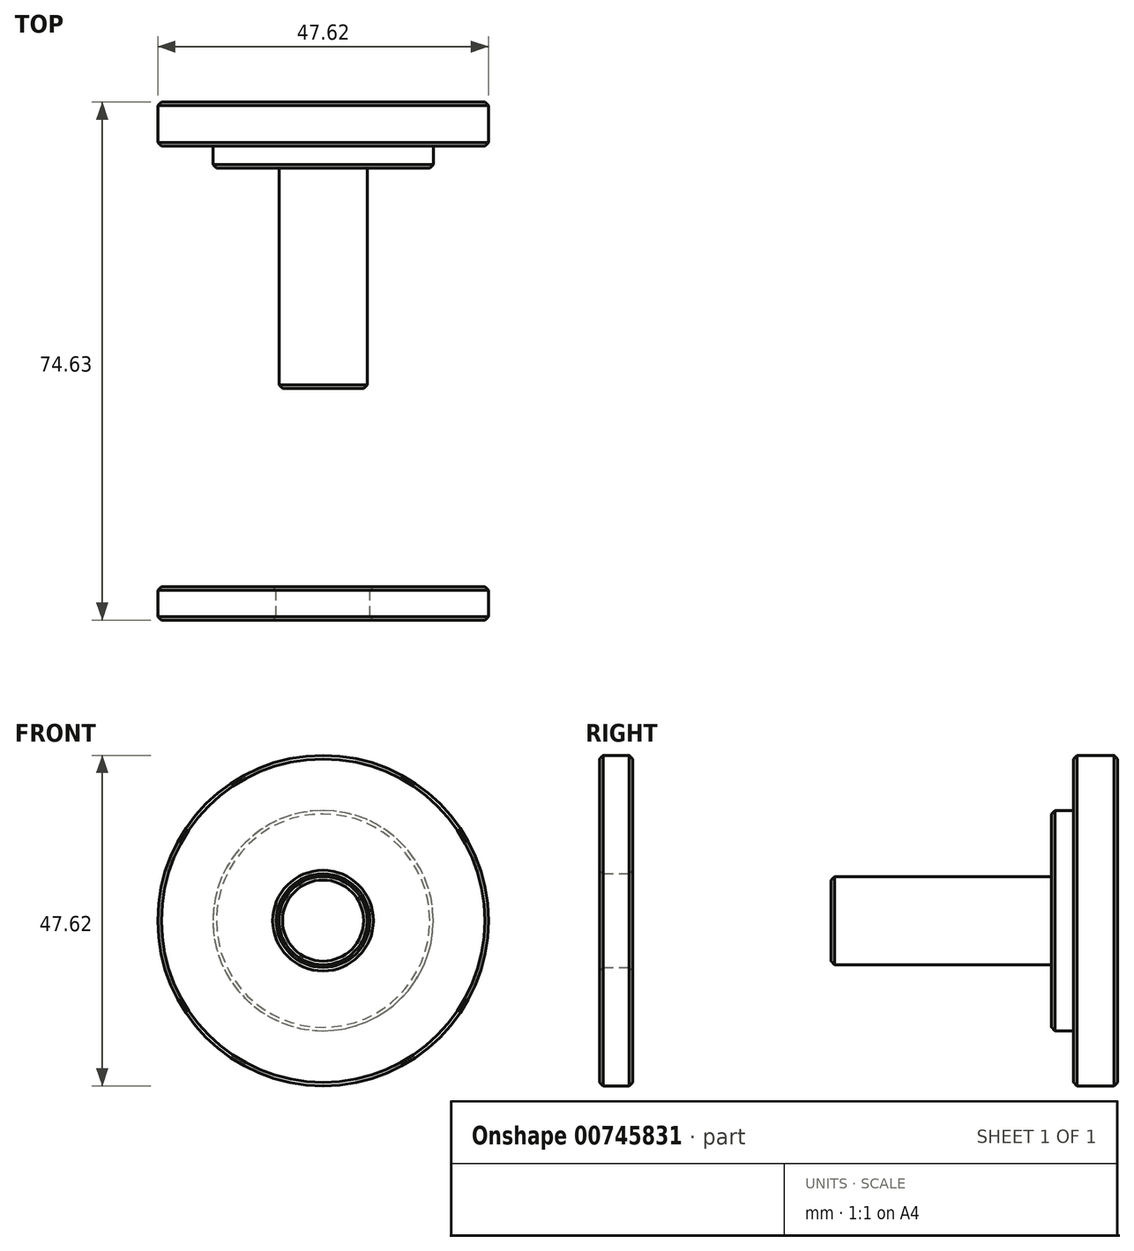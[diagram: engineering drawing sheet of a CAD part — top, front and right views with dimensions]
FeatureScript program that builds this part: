
annotation { "Feature Type Name" : "Feature", "Feature Type Description" : "" }
export const myFeature = defineFeature(function(context is Context, id is Id, definition is map)
    precondition{}
    {
        {
            var Q0;
            Q0=qCreatedBy(makeId("Top.planeOp"),FACE);
            var sketch = newSketch(context, id + "F0", { "sketchPlane" : qUnion([Q0])});
            skLineSegment(sketch, "E0", {"start": v(0, 34.93) * mm, "end": v(0, 0) * mm, "construction": true});
            skLineSegment(sketch, "E1", {"start": v(0, 0) * mm, "end": v(23.81, 0) * mm});
            skLineSegment(sketch, "E2", {"start": v(23.81, 0) * mm, "end": v(23.81, -6.35) * mm});
            skLineSegment(sketch, "E3", {"start": v(23.81, -6.35) * mm, "end": v(15.88, -6.35) * mm});
            skLineSegment(sketch, "E4", {"start": v(15.88, -6.35) * mm, "end": v(15.88, -9.53) * mm});
            skLineSegment(sketch, "E5", {"start": v(15.88, -9.53) * mm, "end": v(6.35, -9.53) * mm});
            skLineSegment(sketch, "E6", {"start": v(6.35, -9.53) * mm, "end": v(6.35, -41.28) * mm});
            skLineSegment(sketch, "E7", {"start": v(6.35, -41.28) * mm, "end": v(0, -41.28) * mm});
            skLineSegment(sketch, "E8", {"start": v(0, -41.28) * mm, "end": v(0, 0) * mm});
            skSolve(sketch);
        }
        {
            var Q0;
            Q0 = qSketchRegion(id + "F0", true);
            var Q1;
            Q1=sQuery(id+"F0.wireOp",EDGE,"E0");
            revolve(context, id + "F1", {"surfaceOperationType" : NewSurfaceOperationType.NEW, "entities" : qUnion([Q0]), "axis" : qUnion([Q1]), "revolveType" : RevolveType.FULL});
        }
        {
            var Q0;
            Q0=qCreatedBy(makeId("Top.planeOp"),FACE);
            var sketch = newSketch(context, id + "F2", { "sketchPlane" : qUnion([Q0])});
            skLineSegment(sketch, "E9", {"start": v(0, -30.05) * mm, "end": v(0, -63.76) * mm, "construction": true});
            skLineSegment(sketch, "E10.bottom", {"start": v(6.74, -69.85) * mm, "end": v(23.81, -69.85) * mm});
            skLineSegment(sketch, "E10.top", {"start": v(6.74, -74.63) * mm, "end": v(23.81, -74.63) * mm});
            skLineSegment(sketch, "E10.left", {"start": v(6.74, -69.85) * mm, "end": v(6.74, -74.63) * mm});
            skLineSegment(sketch, "E10.right", {"start": v(23.81, -69.85) * mm, "end": v(23.81, -74.63) * mm});
            skSolve(sketch);
        }
        {
            var Q0;
            Q0 = qSketchRegion(id + "F2", true);
            var Q1;
            Q1=sQuery(id+"F2.wireOp",EDGE,"E9");
            revolve(context, id + "F3", {"surfaceOperationType" : NewSurfaceOperationType.NEW, "entities" : qUnion([Q0]), "axis" : qUnion([Q1]), "revolveType" : RevolveType.FULL});
        }
        {
            var Q0;
            Q0=makeQuery(id+"F1.opRevolve","SWEPT_EDGE",EDGE,{"disambiguationData":[OSD([sQuery(id+"F0.wireOp",EDGE,"E1"),sQuery(id+"F0.wireOp",EDGE,"E2")])]});
            var Q1;
            Q1=makeQuery(id+"F1.opRevolve","SWEPT_EDGE",EDGE,{"disambiguationData":[OSD([sQuery(id+"F0.wireOp",EDGE,"E2"),sQuery(id+"F0.wireOp",EDGE,"E3")])]});
            var Q2;
            Q2=makeQuery(id+"F1.opRevolve","SWEPT_EDGE",EDGE,{"disambiguationData":[OSD([sQuery(id+"F0.wireOp",EDGE,"E4"),sQuery(id+"F0.wireOp",EDGE,"E5")])]});
            var Q3;
            Q3=makeQuery(id+"F1.opRevolve","SWEPT_EDGE",EDGE,{"disambiguationData":[OSD([sQuery(id+"F0.wireOp",EDGE,"E6"),sQuery(id+"F0.wireOp",EDGE,"E7")])]});
            var Q4;
            Q4=makeQuery(id+"F3.opRevolve","SWEPT_EDGE",EDGE,{"disambiguationData":[OSD([sQuery(id+"F2.wireOp",EDGE,"E10.bottom"),sQuery(id+"F2.wireOp",EDGE,"E10.right")])]});
            var Q5;
            Q5=makeQuery(id+"F3.opRevolve","SWEPT_EDGE",EDGE,{"disambiguationData":[OSD([sQuery(id+"F2.wireOp",EDGE,"E10.top"),sQuery(id+"F2.wireOp",EDGE,"E10.right")])]});
            var Q6;
            Q6=makeQuery(id+"F3.opRevolve","SWEPT_EDGE",EDGE,{"disambiguationData":[OSD([sQuery(id+"F2.wireOp",EDGE,"E10.top"),sQuery(id+"F2.wireOp",EDGE,"E10.left")])]});
            var Q7;
            Q7=makeQuery(id+"F3.opRevolve","SWEPT_EDGE",EDGE,{"disambiguationData":[OSD([sQuery(id+"F2.wireOp",EDGE,"E10.bottom"),sQuery(id+"F2.wireOp",EDGE,"E10.left")])]});
            chamfer(context, id + "F4", {"entities" : qUnion([Q0, Q1, Q2, Q3, Q4, Q5, Q6, Q7]), "width" : 0.5 * mm, "tangentPropagation" : true});
        }
    });
